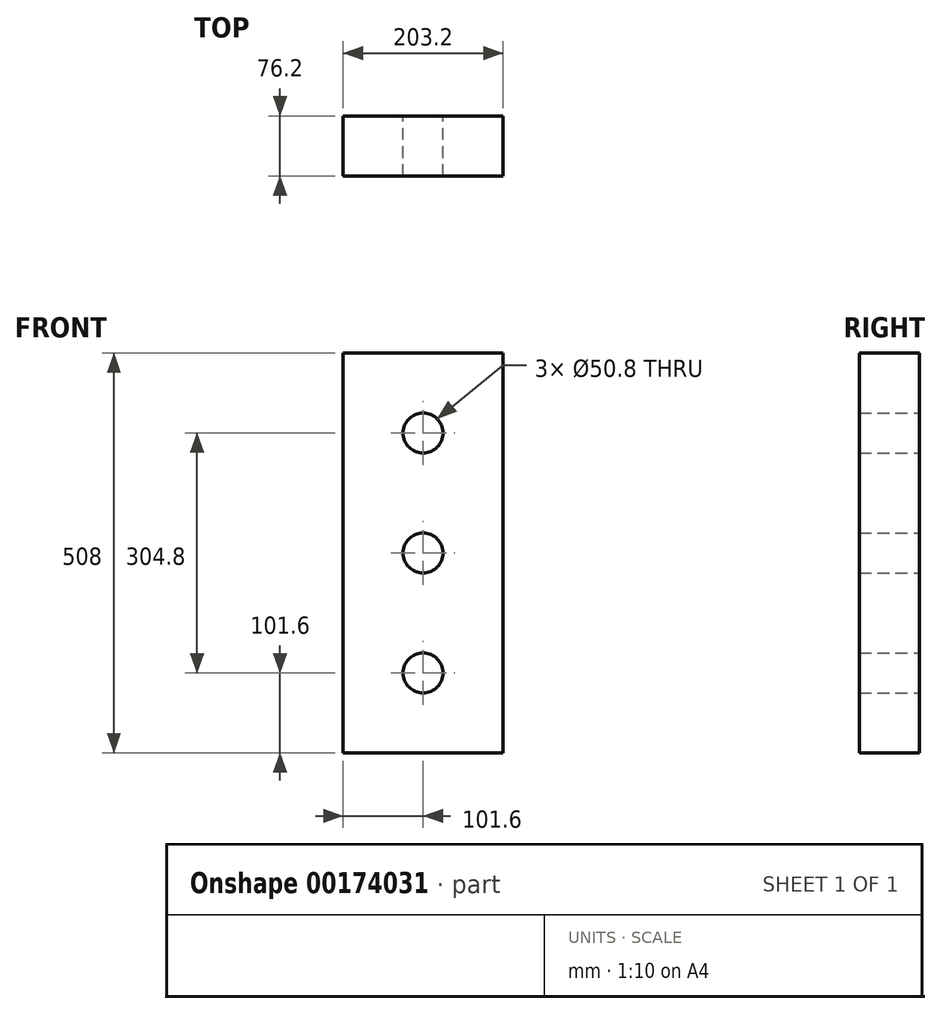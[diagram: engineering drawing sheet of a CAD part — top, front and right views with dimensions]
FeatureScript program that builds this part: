
annotation { "Feature Type Name" : "Feature", "Feature Type Description" : "" }
export const myFeature = defineFeature(function(context is Context, id is Id, definition is map)
    precondition{}
    {
        {
            var Q0;
            Q0=qCreatedBy(makeId("Front.planeOp"),FACE);
            var sketch = newSketch(context, id + "F0", { "sketchPlane" : qUnion([Q0])});
            skLineSegment(sketch, "E0.bottom", {"start": v(101.6, 254) * mm, "end": v(-101.6, 254) * mm});
            skLineSegment(sketch, "E0.top", {"start": v(101.6, -254) * mm, "end": v(-101.6, -254) * mm});
            skLineSegment(sketch, "E0.left", {"start": v(101.6, 254) * mm, "end": v(101.6, -254) * mm});
            skLineSegment(sketch, "E0.right", {"start": v(-101.6, 254) * mm, "end": v(-101.6, -254) * mm});
            skPoint(sketch, "E0.middle", {"position": v(0, 0) * mm});
            skCircle(sketch, "E1", {"center": v(0, 0) * mm, "radius": 25.4 * mm});
            skCircle(sketch, "E2", {"center": v(0, 152.4) * mm, "radius": 25.4 * mm});
            skCircle(sketch, "E3", {"center": v(0, -152.4) * mm, "radius": 25.4 * mm});
            skSolve(sketch);
        }
        {
            var Q0;
            Q0=makeQuery(id+"F0.imprint","IMPRINT",FACE,{"disambiguationData":[TD([[makeQuery(id+"F0.imprint","IMPRINT",EDGE,{"derivedFrom":sQuery(id+"F0.wireOp",EDGE,"E0.bottom")}),1.0]])]});
            extrude(context, id + "F1", {"entities" : qUnion([Q0]), "endBound" : BoundingType.SYMMETRIC, "depth" : 76.2 * mm});
        }
    });
